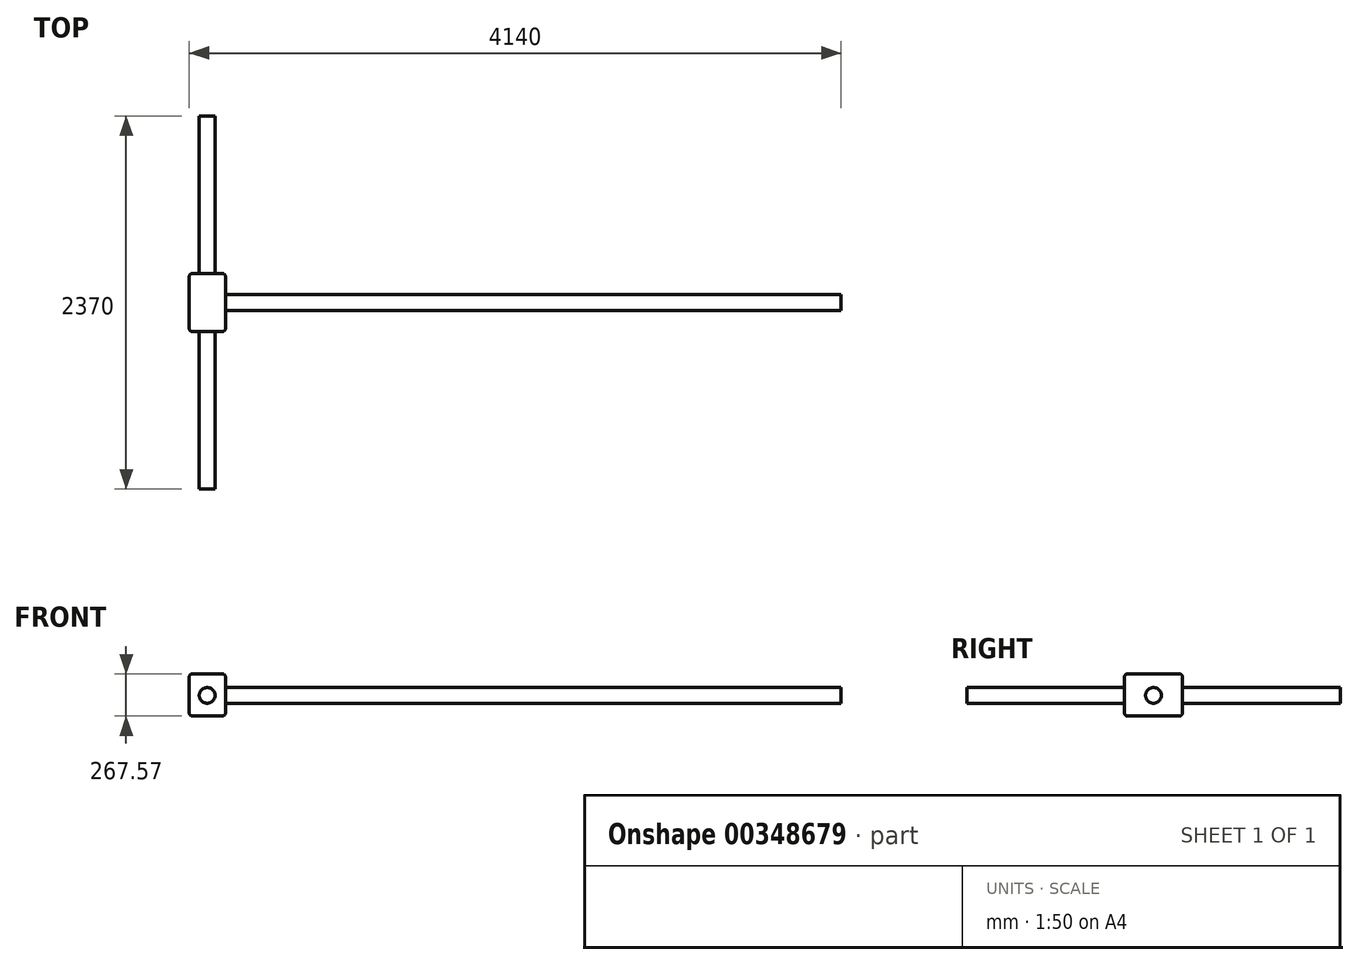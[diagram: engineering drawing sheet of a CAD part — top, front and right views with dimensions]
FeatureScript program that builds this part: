
annotation { "Feature Type Name" : "Feature", "Feature Type Description" : "" }
export const myFeature = defineFeature(function(context is Context, id is Id, definition is map)
    precondition{}
    {
        {
            var Q0;
            Q0=qCreatedBy(makeId("Right.planeOp"),FACE);
            var sketch = newSketch(context, id + "F0", { "sketchPlane" : qUnion([Q0])});
            skCircle(sketch, "E0", {"center": v(0, 0) * mm, "radius": 50 * mm});
            skSolve(sketch);
        }
        {
            var Q0;
            Q0 = qSketchRegion(id + "F0", true);
            extrude(context, id + "F1", {"entities" : qUnion([Q0]), "depth" : 3910 * mm});
        }
        {
            var Q0;
            Q0=makeQuery(id+"F1.opExtrude","CAP_FACE",FACE,{"disambiguationData":[OSD([sQuery(id+"F0.wireOp",EDGE,"E0")])],"isStart":true});
            var sketch = newSketch(context, id + "F2", { "sketchPlane" : qUnion([Q0])});
            skLineSegment(sketch, "E1", {"start": v(0, 0) * mm, "end": v(0, -131.12) * mm});
            skLineSegment(sketch, "E2", {"start": v(0, 0) * mm, "end": v(0, 8.01) * mm});
            skLineSegment(sketch, "E3", {"start": v(0, 136.45) * mm, "end": v(0, 8.01) * mm});
            skLineSegment(sketch, "E4", {"start": v(0, 136.45) * mm, "end": v(-184.14, 136.45) * mm});
            skLineSegment(sketch, "E5", {"start": v(-184.14, 136.45) * mm, "end": v(-184.14, -131.12) * mm});
            skLineSegment(sketch, "E6", {"start": v(-184.14, -131.12) * mm, "end": v(0, -131.12) * mm});
            skLineSegment(sketch, "E7", {"start": v(0, -131.12) * mm, "end": v(184, -131.12) * mm});
            skLineSegment(sketch, "E8", {"start": v(184, -131.12) * mm, "end": v(184, 136.45) * mm});
            skLineSegment(sketch, "E9", {"start": v(184, 136.45) * mm, "end": v(0, 136.45) * mm});
            skSolve(sketch);
        }
        {
            var Q0;
            Q0 = qSketchRegion(id + "F2", true);
            extrude(context, id + "F3", {"entities" : qUnion([Q0]), "operationType" : NewBodyOperationType.ADD, "depth" : 230 * mm});
        }
        {
            var Q0;
            Q0=makeQuery(id+"F3.opExtrude","SWEPT_FACE",FACE,{"disambiguationData":[OSD([sQuery(id+"F2.wireOp",EDGE,"E4"),sQuery(id+"F2.wireOp",EDGE,"E9")])]});
            var Q1;
            Q1=makeQuery(id+"F3.opExtrude","SWEPT_FACE",FACE,{"disambiguationData":[OSD([sQuery(id+"F2.wireOp",EDGE,"E8")])]});
            var Q2;
            Q2=makeQuery(id+"F3.opExtrude","CAP_FACE",FACE,{"disambiguationData":[OSD([sQuery(id+"F2.wireOp",EDGE,"E4"),sQuery(id+"F2.wireOp",EDGE,"E5"),sQuery(id+"F2.wireOp",EDGE,"E6"),sQuery(id+"F2.wireOp",EDGE,"E7"),sQuery(id+"F2.wireOp",EDGE,"E8"),sQuery(id+"F2.wireOp",EDGE,"E9")])],"isStart":false});
            var Q3;
            Q3=makeQuery(id+"F3.opExtrude","SWEPT_FACE",FACE,{"disambiguationData":[OSD([sQuery(id+"F2.wireOp",EDGE,"E6"),sQuery(id+"F2.wireOp",EDGE,"E7")])]});
            var Q4;
            Q4=makeQuery(id+"F3.opExtrude","CAP_FACE",FACE,{"disambiguationData":[OSD([sQuery(id+"F2.wireOp",EDGE,"E4"),sQuery(id+"F2.wireOp",EDGE,"E5"),sQuery(id+"F2.wireOp",EDGE,"E6"),sQuery(id+"F2.wireOp",EDGE,"E7"),sQuery(id+"F2.wireOp",EDGE,"E8"),sQuery(id+"F2.wireOp",EDGE,"E9")])],"isStart":true});
            var Q5;
            Q5=makeQuery(id+"F3.opExtrude","SWEPT_FACE",FACE,{"disambiguationData":[OSD([sQuery(id+"F2.wireOp",EDGE,"E5")])]});
            fillet(context, id + "F4", {"entities" : qUnion([Q0, Q1, Q2, Q3, Q4, Q5]), "radius" : 20 * mm, "tangentPropagation" : true, "allowEdgeOverflow" : false});
        }
        {
            var Q0;
            Q0=makeQuery(id+"F3.opExtrude","SWEPT_FACE",FACE,{"disambiguationData":[OSD([sQuery(id+"F2.wireOp",EDGE,"E8")])]});
            var sketch = newSketch(context, id + "F5", { "sketchPlane" : qUnion([Q0])});
            skCircle(sketch, "E10", {"center": v(-116.09, 0) * mm, "radius": 50 * mm});
            skSolve(sketch);
        }
        {
            var Q0;
            Q0 = qSketchRegion(id + "F5", true);
            extrude(context, id + "F6", {"entities" : qUnion([Q0]), "operationType" : NewBodyOperationType.ADD, "depth" : 1000 * mm});
        }
        {
            var Q0;
            Q0=makeQuery(id+"F6.opExtrude","CAP_FACE",FACE,{"disambiguationData":[OSD([sQuery(id+"F5.wireOp",EDGE,"E10")])],"isStart":false});
            extrude(context, id + "F7", {"entities" : qUnion([Q0]), "operationType" : NewBodyOperationType.ADD, "oppositeDirection" : true, "depth" : 1370 * mm});
        }
        {
            var Q0;
            Q0=makeQuery(id+"F7.opExtrude","CAP_FACE",FACE,{"disambiguationData":[OSD([sQuery(id+"F5.wireOp",EDGE,"E10")])],"isStart":false});
            extrude(context, id + "F8", {"entities" : qUnion([Q0]), "operationType" : NewBodyOperationType.ADD, "depth" : 1000 * mm});
        }
    });
